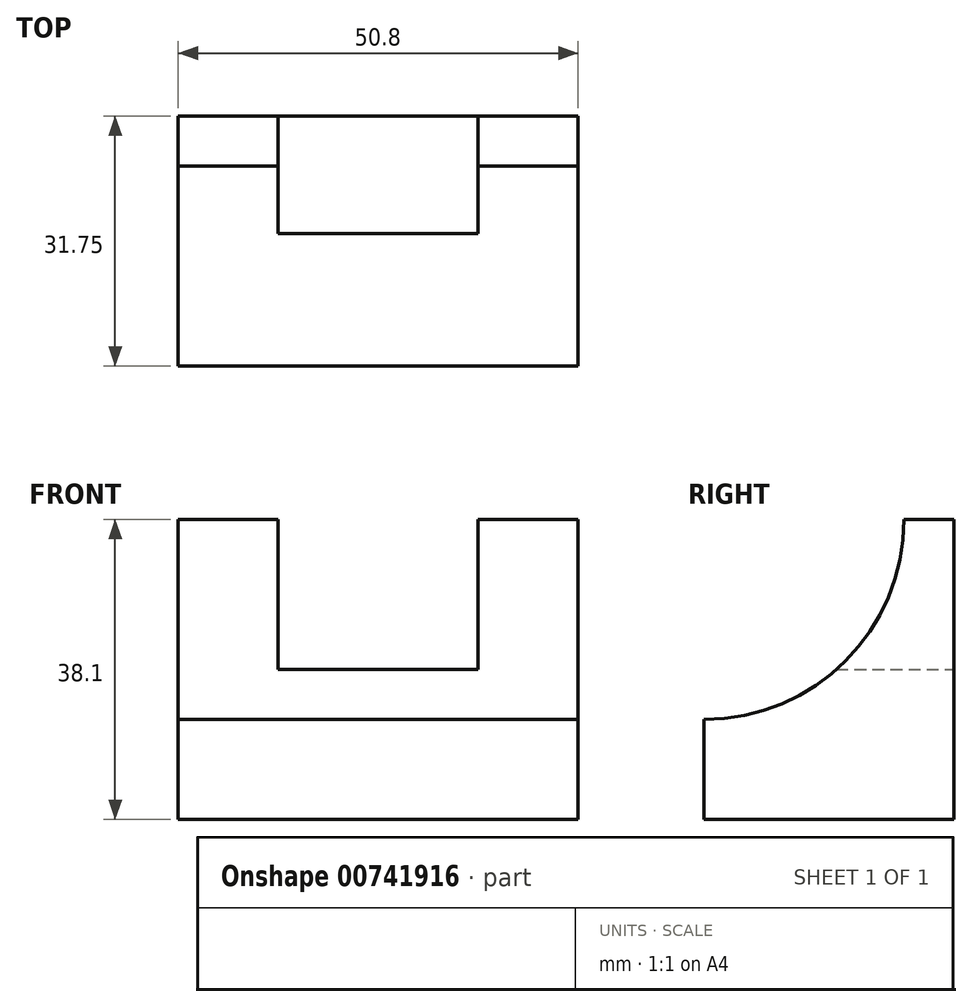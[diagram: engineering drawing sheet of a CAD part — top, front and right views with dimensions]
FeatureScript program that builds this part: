
annotation { "Feature Type Name" : "Feature", "Feature Type Description" : "" }
export const myFeature = defineFeature(function(context is Context, id is Id, definition is map)
    precondition{}
    {
        {
            var Q0;
            Q0=qCreatedBy(makeId("Right.planeOp"),FACE);
            var sketch = newSketch(context, id + "F0", { "sketchPlane" : qUnion([Q0])});
            skLineSegment(sketch, "E0", {"start": v(0, 0) * mm, "end": v(0, 38.1) * mm});
            skLineSegment(sketch, "E1", {"start": v(0, 38.1) * mm, "end": v(31.75, 38.1) * mm});
            skLineSegment(sketch, "E2", {"start": v(31.75, 38.1) * mm, "end": v(31.75, 0) * mm});
            skLineSegment(sketch, "E3", {"start": v(31.75, 0) * mm, "end": v(0, 0) * mm});
            skSolve(sketch);
        }
        {
            var Q0;
            Q0=makeQuery(id+"F0.imprint","IMPRINT",FACE,{"disambiguationData":[TD([[makeQuery(id+"F0.imprint","IMPRINT",EDGE,{"derivedFrom":sQuery(id+"F0.wireOp",EDGE,"E0")}),-1.0]])]});
            extrude(context, id + "F1", {"entities" : qUnion([Q0]), "depth" : 50.8 * mm, "offsetDistance" : 25.4 * mm});
        }
        {
            var Q0;
            Q0=makeQuery(id+"F1.opExtrude","CAP_FACE",FACE,{"disambiguationData":[OSD([sQuery(id+"F0.wireOp",EDGE,"E0"),sQuery(id+"F0.wireOp",EDGE,"E1"),sQuery(id+"F0.wireOp",EDGE,"E2"),sQuery(id+"F0.wireOp",EDGE,"E3")])],"isStart":false});
            var sketch = newSketch(context, id + "F2", { "sketchPlane" : qUnion([Q0])});
            skCircle(sketch, "E4", {"center": v(0, 38.1) * mm, "radius": 25.4 * mm});
            skLineSegment(sketch, "E5", {"start": v(31.75, 38.1) * mm, "end": v(25.4, 38.1) * mm});
            skSolve(sketch);
        }
        {
            var Q0;
            {var subQ0=sQuery(id+"F2.wireOp",EDGE,"I00cAV3t-wref-Bd4o-ctTZ-uB9PCzsgoOcg");Q0=makeQuery(id+"F2.imprint","IMPRINT",FACE,{"disambiguationData":[TD([[makeQuery(id+"F2.imprint","IMPRINT",EDGE,{"derivedFrom":subQ0}),1.0]])]});}
            var Q1;
            {var subQ1=makeQuery(id+"F1.opExtrude","CAP_EDGE",EDGE,{"disambiguationData":[OSD([sQuery(id+"F0.wireOp",EDGE,"E1")])],"isStart":false});var subQ3=makeQuery(id+"F1.opExtrude","CAP_EDGE",EDGE,{"disambiguationData":[OSD([sQuery(id+"F0.wireOp",EDGE,"E0")])],"isStart":false});var subQ5=makeQuery(id+"F2.imprint","INTERSECT",VERTEX,{"derivedFrom":[subQ3,subQ1]});Q1=makeQuery(id+"F2.imprint","IMPRINT",FACE,{"disambiguationData":[TD([[makeQuery(id+"F2.imprint","IMPRINT",EDGE,{"disambiguationData":[TD([[subQ5,1.0]])],"derivedFrom":subQ3}),1.0]])]});}
            var Q2;
            {var subQ1=makeQuery(id+"F1.opExtrude","CAP_EDGE",EDGE,{"disambiguationData":[OSD([sQuery(id+"F0.wireOp",EDGE,"E1")])],"isStart":false});var subQ3=makeQuery(id+"F1.opExtrude","CAP_EDGE",EDGE,{"disambiguationData":[OSD([sQuery(id+"F0.wireOp",EDGE,"E0")])],"isStart":false});var subQ5=makeQuery(id+"F2.imprint","INTERSECT",VERTEX,{"derivedFrom":[subQ3,subQ1]});Q2=makeQuery(id+"F2.imprint","IMPRINT",FACE,{"disambiguationData":[TD([[makeQuery(id+"F2.imprint","IMPRINT",EDGE,{"disambiguationData":[TD([[subQ5,1.0]])],"derivedFrom":subQ3}),-1.0]])]});}
            extrude(context, id + "F3", {"entities" : qUnion([Q0, Q1, Q2]), "operationType" : NewBodyOperationType.REMOVE, "endBound" : BoundingType.THROUGH_ALL, "oppositeDirection" : true, "depth" : 25.4 * mm, "offsetDistance" : 25.4 * mm});
        }
        {
            var Q0;
            Q0=makeQuery(id+"F1.opExtrude","SWEPT_FACE",FACE,{"disambiguationData":[OSD([sQuery(id+"F0.wireOp",EDGE,"E2")])]});
            var sketch = newSketch(context, id + "F4", { "sketchPlane" : qUnion([Q0])});
            skLineSegment(sketch, "E6", {"start": v(-38.1, 38.1) * mm, "end": v(-38.1, 19.05) * mm});
            skLineSegment(sketch, "E7", {"start": v(-38.1, 19.05) * mm, "end": v(-12.7, 19.05) * mm});
            skLineSegment(sketch, "E8", {"start": v(-12.7, 19.05) * mm, "end": v(-12.7, 38.1) * mm});
            skLineSegment(sketch, "E9", {"start": v(-12.7, 38.1) * mm, "end": v(-38.1, 38.1) * mm});
            skSolve(sketch);
        }
        {
            var Q0;
            Q0=makeQuery(id+"F4.imprint","IMPRINT",FACE,{"disambiguationData":[TD([[makeQuery(id+"F4.imprint","IMPRINT",EDGE,{"derivedFrom":sQuery(id+"F4.wireOp",EDGE,"E6")}),1.0]])]});
            extrude(context, id + "F5", {"entities" : qUnion([Q0]), "operationType" : NewBodyOperationType.REMOVE, "endBound" : BoundingType.THROUGH_ALL, "oppositeDirection" : true, "depth" : 25.4 * mm, "offsetDistance" : 25.4 * mm});
        }
    });
